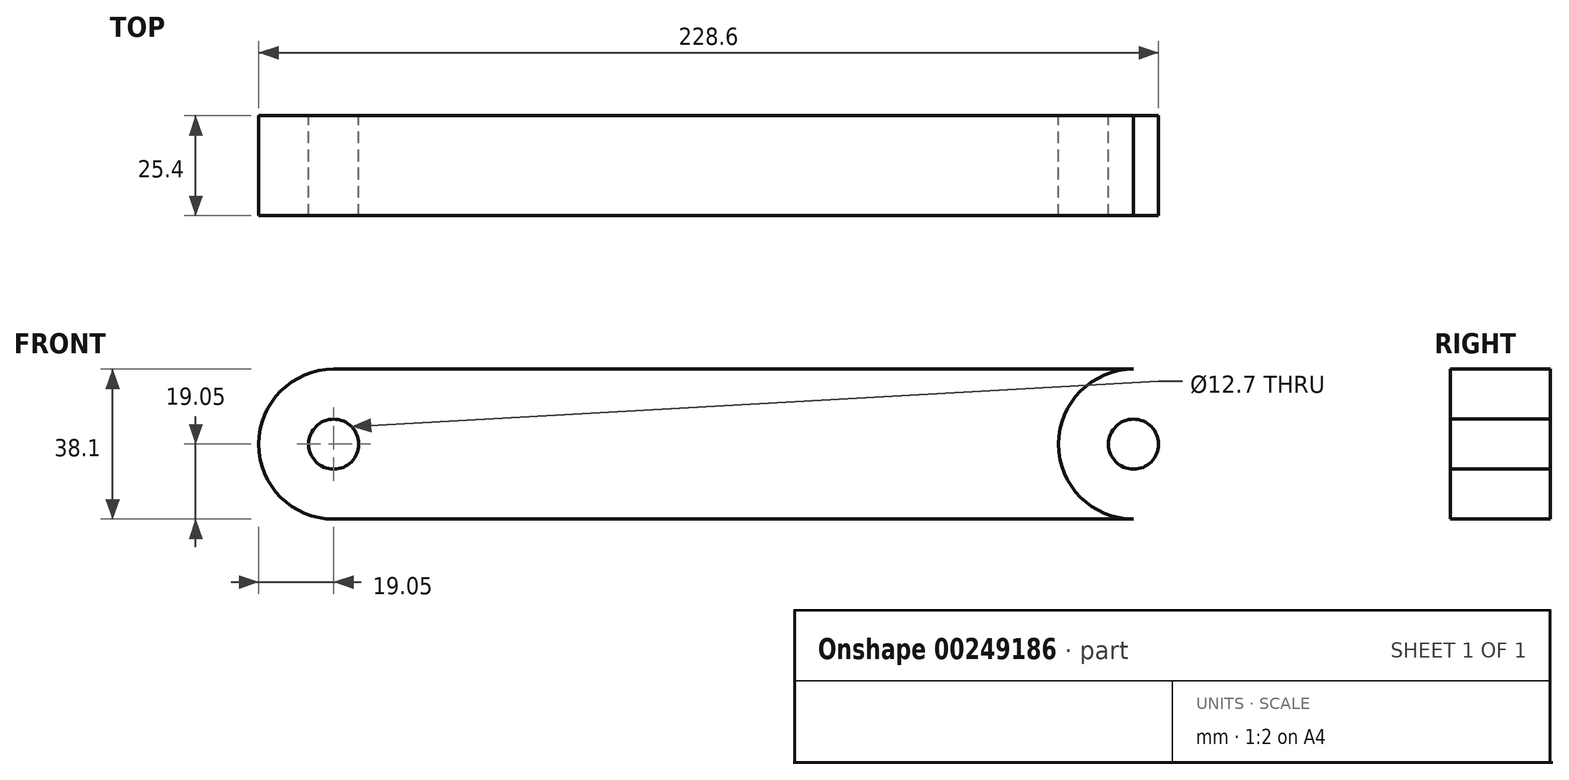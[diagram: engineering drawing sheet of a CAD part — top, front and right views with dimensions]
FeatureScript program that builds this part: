
annotation { "Feature Type Name" : "Feature", "Feature Type Description" : "" }
export const myFeature = defineFeature(function(context is Context, id is Id, definition is map)
    precondition{}
    {
        {
            var Q0;
            Q0=qCreatedBy(makeId("Front.planeOp"),FACE);
            var sketch = newSketch(context, id + "F0", { "sketchPlane" : qUnion([Q0])});
            skCircle(sketch, "E0", {"center": v(-101.6, 0) * mm, "radius": 19.05 * mm});
            skCircle(sketch, "E1", {"center": v(-101.6, 0) * mm, "radius": 6.35 * mm});
            skCircle(sketch, "E2.MirrorC", {"center": v(101.6, 0) * mm, "radius": 19.05 * mm});
            skCircle(sketch, "E3.MirrorC", {"center": v(101.6, 0) * mm, "radius": 6.35 * mm});
            skLineSegment(sketch, "E4", {"start": v(-101.6, -19.05) * mm, "end": v(101.6, -19.05) * mm});
            skLineSegment(sketch, "E5", {"start": v(-101.6, 19.05) * mm, "end": v(101.6, 19.05) * mm});
            skSolve(sketch);
        }
        {
            var Q0;
            {var subQ0=sQuery(id+"F0.wireOp",EDGE,"E4");Q0=makeQuery(id+"F0.imprint","IMPRINT",FACE,{"disambiguationData":[TD([[makeQuery(id+"F0.imprint","IMPRINT",EDGE,{"derivedFrom":subQ0}),1.0]])]});}
            var Q1;
            Q1=makeQuery(id+"F0.imprint","IMPRINT",FACE,{"disambiguationData":[TD([[makeQuery(id+"F0.imprint","IMPRINT",EDGE,{"derivedFrom":sQuery(id+"F0.wireOp",EDGE,"E1")}),-1.0]])]});
            var Q2;
            Q2=makeQuery(id+"F0.imprint","IMPRINT",FACE,{"disambiguationData":[TD([[makeQuery(id+"F0.imprint","IMPRINT",EDGE,{"derivedFrom":sQuery(id+"F0.wireOp",EDGE,"E3.MirrorC")}),1.0]])]});
            extrude(context, id + "F1", {"entities" : qUnion([Q0, Q1, Q2]), "depth" : 25.4 * mm});
        }
    });
